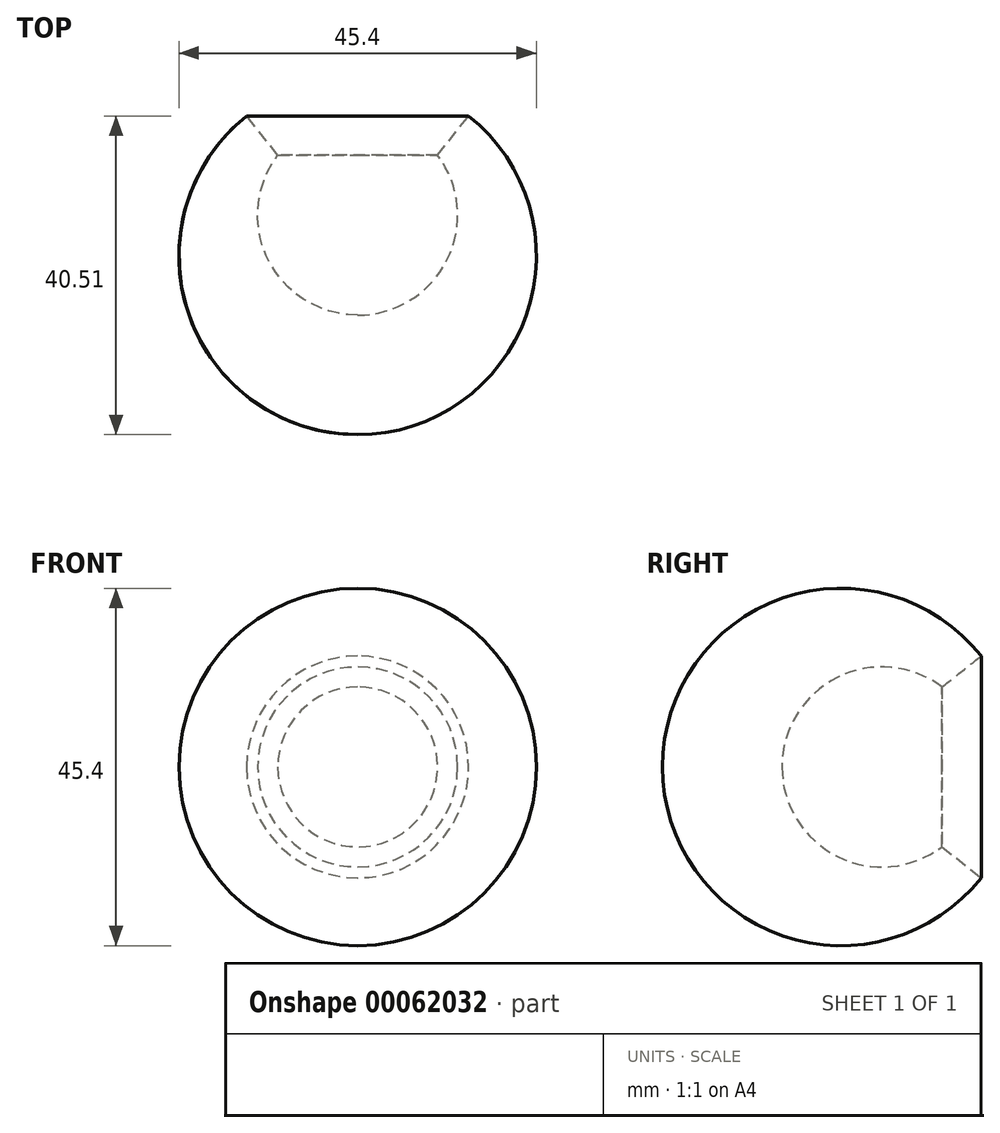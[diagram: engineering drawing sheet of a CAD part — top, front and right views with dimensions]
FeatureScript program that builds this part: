
annotation { "Feature Type Name" : "Feature", "Feature Type Description" : "" }
export const myFeature = defineFeature(function(context is Context, id is Id, definition is map)
    precondition{}
    {
        {
            var Q0;
            Q0=qCreatedBy(makeId("Top.planeOp"),FACE);
            var sketch = newSketch(context, id + "F0", { "sketchPlane" : qUnion([Q0])});
            skArc(sketch, "E0", {"start": v(-6.35, 11) * mm, "mid": v(0, -12.7) * mm, "end": v(6.35, 11) * mm});
            skLineSegment(sketch, "E1", {"start": v(-6.35, 11) * mm, "end": v(6.35, 11) * mm});
            skPoint(sketch, "E2.0.midPoint", {"position": v(0, -22.37) * mm});
            skPoint(sketch, "E3.orphan", {"position": v(0, 29.5) * mm});
            skArc(sketch, "E4", {"start": v(-10.15, 7.63) * mm, "mid": v(0, -21.55) * mm, "end": v(10.15, 7.63) * mm});
            skArc(sketch, "E5.0", {"start": v(-14.1, 12.6) * mm, "mid": v(0, -27.9) * mm, "end": v(14.1, 12.6) * mm});
            skLineSegment(sketch, "E6", {"start": v(-14.1, 12.6) * mm, "end": v(-10.15, 7.63) * mm});
            skLineSegment(sketch, "E7", {"start": v(14.1, 12.6) * mm, "end": v(10.15, 7.63) * mm});
            skLineSegment(sketch, "E8", {"start": v(0, 11) * mm, "end": v(0, -27.9) * mm});
            skSolve(sketch);
        }
        {
            var Q0;
            {var subQ0=sQuery(id+"F0.wireOp",EDGE,"E4");var subQ1=sQuery(id+"F0.wireOp",EDGE,"E0");var subQ2=makeQuery(id+"F0.imprint","INTERSECT",VERTEX,{"disambiguationData":[OD(0.0)],"derivedFrom":[subQ1,subQ0]});Q0=makeQuery(id+"F0.imprint","IMPRINT",FACE,{"disambiguationData":[TD([[makeQuery(id+"F0.imprint","IMPRINT",EDGE,{"disambiguationData":[TD([[subQ2,-1.0]])],"derivedFrom":subQ1}),-1.0]])]});}
            var Q1;
            {var subQ0=sQuery(id+"F0.wireOp",EDGE,"E6");Q1=makeQuery(id+"F0.imprint","IMPRINT",FACE,{"disambiguationData":[TD([[makeQuery(id+"F0.imprint","IMPRINT",EDGE,{"derivedFrom":subQ0}),-1.0]])]});}
            var Q2;
            Q2=sQuery(id+"F0.wireOp",EDGE,"E8");
            revolve(context, id + "F1", {"entities" : qUnion([Q0, Q1]), "axis" : qUnion([Q2]), "revolveType" : RevolveType.FULL});
        }
    });
